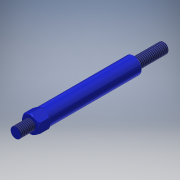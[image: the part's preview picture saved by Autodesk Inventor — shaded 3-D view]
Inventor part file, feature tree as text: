
AUTODESK INVENTOR PART (.ipt)
format: ipt  version: 2018 (Build 220112000, 112)  size: 162,304 bytes
history: native  units: mm
features: sketch x4, extrude x4, thread x2, revolve x1
ambient origin geometry x8: Origin, YZ Plane, XZ Plane, XY Plane, X Axis, Y Axis, Z Axis, Center Point
bodies: Solid1 (feature_tree)
feature tree (11):
  sketch  "Sketch1"  dims[d0=8.0mm d1=6.0mm d2=0.0mm]
  extrude  "Extrusion1"  Depth=6.0mm TaperAngle=0.0deg
  extrude  "Extrusion2"  Depth=6.0mm
  extrude  "Extrusion3"  Depth=2.5mm
  revolve  "Revolution1"  [1 undecoded]
  extrude  "Extrusion4"  Depth=10.0mm
  thread  "Thread1"  [1 undecoded]
  thread  "Thread2"  [1 undecoded]
  sketch  "Sketch2"  dims[d3=6.0mm d4=6.108652mm d5=6.0mm d6=6.108652mm]
  sketch  "Sketch3"  dims[d7=4.0mm d8=2.5mm]
  sketch  "Sketch4"  dims[d9=44.0mm d10=15.0mm d11=0.5mm d12=0.5mm d13=90.0deg d14=5.0mm d15=7.0mm d16=0.0mm d17=10.0mm d18=0.0mm d19=10.0mm d20=0.0mm]
note: 3 required parameter values undecoded (feature->parameter linkage not recoverable at this tier; creation-order binding heuristic only, values carry confidence <= 0.55)